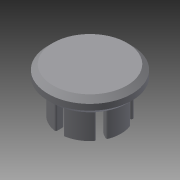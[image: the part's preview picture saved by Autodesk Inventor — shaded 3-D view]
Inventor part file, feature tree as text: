
AUTODESK INVENTOR PART (.ipt)
format: ipt  version: 2014 (Build 180170000, 170)  size: 437,248 bytes
history: native  units: in
note: dims shown in document units (in); Inventor stores cm internally (conversion verified against a paired STEP export)
features: extrude x3, fillet x2, sketch x2, other x1, chamfer x1
ambient origin geometry x8: Origin, YZ Plane, XZ Plane, XY Plane, X Axis, Y Axis, Z Axis, Center Point
bodies: Solid1 (feature_tree)
feature tree (9):
  other  "wheelinsertsketch.ipt"
  extrude  "Extrusion1"  Depth=0.3937in TaperAngle=0.0deg
  extrude  "Extrusion2"  Depth=0.2in TaperAngle=0.0deg
  fillet  "Fillet4"  Radius=0.09in
  chamfer  "Chamfer2"  Distance=0.125in Angle=45.0deg
  extrude  "Extrusion3"  Depth=0.1in TaperAngle=0.0deg
  fillet  "Fillet5"  Radius=0.2in
  sketch  "Sketch1"  dims[d0=0.3937in d1=0.75in d2=0.0in]
  sketch  "Sketch2"  dims[d3=2.15in d4=0.4in d5=0.0in d12=0.09in d13=0.125in d14=0.125in d15=45.0deg d16=0.1in d17=0.0in d18=0.2in]
